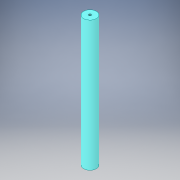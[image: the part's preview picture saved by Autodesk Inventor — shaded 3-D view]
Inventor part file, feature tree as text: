
AUTODESK INVENTOR PART (.ipt)
format: ipt  version: 2018 (Build 220112000, 112)  size: 114,688 bytes
history: native  units: in
note: dims shown in document units (in); Inventor stores cm internally (conversion verified against a paired STEP export)
features: sketch x3, hole x2, extrude x1
ambient origin geometry x8: Origin, YZ Plane, XZ Plane, XY Plane, X Axis, Y Axis, Z Axis, Center Point
bodies: Solid1 (feature_tree)
feature tree (6):
  extrude  "Extrusion1"  Depth=10.229in TaperAngle=0.0deg
  sketch  "Sketch3"  dims[d4=0.196in d5=0.5in d6=0.375in d7=0.25in d8=0.5635in d9=0.75in d10=0.8108in d11=0.5in d12=0.196in d13=0.5in d14=0.375in d15=0.25in d16=0.5635in d17=0.75in d18=0.8108in]
  hole  "Hole1"  [1 undecoded]
  hole  "Hole2"  [1 undecoded]
  sketch  "Sketch1"  dims[d0=1.0in d1=10.229in d2=0.0in]
  sketch  "Sketch2"  dims[d3=0.25in]
note: 2 required parameter values undecoded (feature->parameter linkage not recoverable at this tier; creation-order binding heuristic only, values carry confidence <= 0.55)
